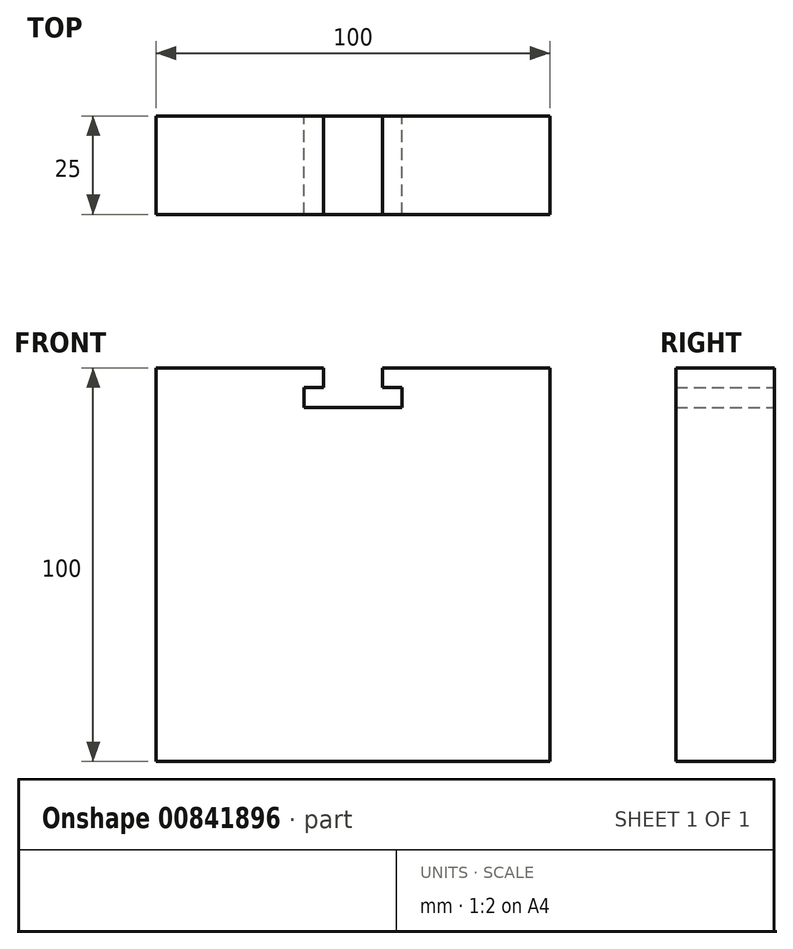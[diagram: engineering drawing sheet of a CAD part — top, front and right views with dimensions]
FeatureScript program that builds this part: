
annotation { "Feature Type Name" : "Feature", "Feature Type Description" : "" }
export const myFeature = defineFeature(function(context is Context, id is Id, definition is map)
    precondition{}
    {
        {
            var Q0;
            Q0=qCreatedBy(makeId("Front.planeOp"),FACE);
            var sketch = newSketch(context, id + "F0", { "sketchPlane" : qUnion([Q0])});
            skLineSegment(sketch, "E0.bottom", {"start": v(50, 50) * mm, "end": v(-50, 50) * mm});
            skLineSegment(sketch, "E0.top", {"start": v(50, -50) * mm, "end": v(-50, -50) * mm});
            skLineSegment(sketch, "E0.left", {"start": v(50, 50) * mm, "end": v(50, -50) * mm});
            skLineSegment(sketch, "E0.right", {"start": v(-50, 50) * mm, "end": v(-50, -50) * mm});
            skPoint(sketch, "E0.middle", {"position": v(0, 0) * mm});
            skSolve(sketch);
        }
        {
            var Q0;
            Q0=qCreatedBy(makeId("Right.planeOp"),FACE);
            var sketch = newSketch(context, id + "F1", { "sketchPlane" : qUnion([Q0])});
            skLineSegment(sketch, "E1", {"start": v(-138.73, 0) * mm, "end": v(143.52, 0) * mm});
            skSolve(sketch);
        }
        {
            var Q0;
            Q0 = qSketchRegion(id + "F0", true);
            extrude(context, id + "F2", {"entities" : qUnion([Q0]), "depth" : 25 * mm, "offsetDistance" : 25 * mm});
        }
        {
            var Q0;
            Q0=qCreatedBy(makeId("Front.planeOp"),FACE);
            var sketch = newSketch(context, id + "F3", { "sketchPlane" : qUnion([Q0])});
            skLineSegment(sketch, "E2.0.0", {"start": v(50, -50) * mm, "end": v(50, 50) * mm, "construction": true});
            skLineSegment(sketch, "E2.0.1", {"start": v(50, 50) * mm, "end": v(-50, 50) * mm, "construction": true});
            skLineSegment(sketch, "E2.0.2", {"start": v(-50, 50) * mm, "end": v(-50, -50) * mm, "construction": true});
            skLineSegment(sketch, "E2.0.3", {"start": v(-50, -50) * mm, "end": v(50, -50) * mm, "construction": true});
            skLineSegment(sketch, "E3", {"start": v(0, -50) * mm, "end": v(0, 50) * mm, "construction": true});
            skLineSegment(sketch, "E4", {"start": v(-50, 0) * mm, "end": v(50, 0) * mm, "construction": true});
            skLineSegment(sketch, "E5", {"start": v(0, 50) * mm, "end": v(-7.5, 50) * mm});
            skLineSegment(sketch, "E6", {"start": v(-7.5, 50) * mm, "end": v(-7.5, 45) * mm});
            skLineSegment(sketch, "E7", {"start": v(-7.5, 45) * mm, "end": v(-12.5, 45) * mm});
            skLineSegment(sketch, "E8", {"start": v(-12.5, 45) * mm, "end": v(-12.5, 40) * mm});
            skLineSegment(sketch, "E9", {"start": v(-12.5, 40) * mm, "end": v(0, 40) * mm});
            skLineSegment(sketch, "E10.MirrorCS", {"start": v(12.5, 40) * mm, "end": v(0, 40) * mm});
            skLineSegment(sketch, "E11.MirrorCS", {"start": v(12.5, 45) * mm, "end": v(12.5, 40) * mm});
            skLineSegment(sketch, "E12.MirrorCS", {"start": v(7.5, 45) * mm, "end": v(12.5, 45) * mm});
            skLineSegment(sketch, "E13.MirrorCS", {"start": v(7.5, 50) * mm, "end": v(7.5, 45) * mm});
            skLineSegment(sketch, "E14.MirrorCS", {"start": v(0, 50) * mm, "end": v(7.5, 50) * mm});
            skSolve(sketch);
        }
        {
            var Q0;
            Q0 = qSketchRegion(id + "F3", true);
            extrude(context, id + "F4", {"entities" : qUnion([Q0]), "operationType" : NewBodyOperationType.REMOVE, "endBound" : BoundingType.THROUGH_ALL, "depth" : 25 * mm, "offsetDistance" : 25 * mm});
        }
    });
